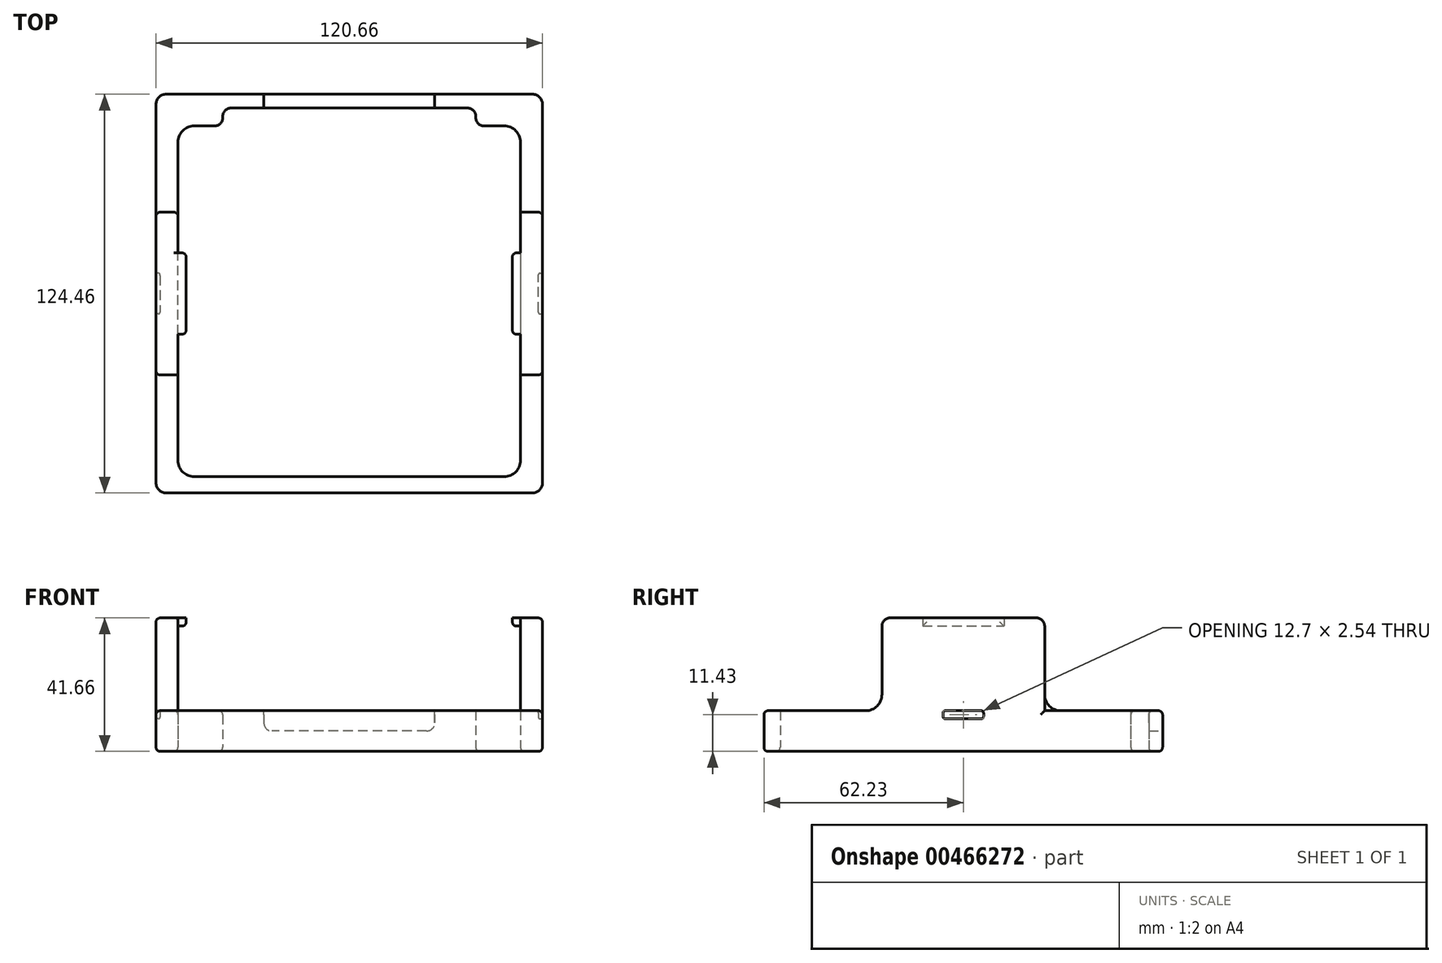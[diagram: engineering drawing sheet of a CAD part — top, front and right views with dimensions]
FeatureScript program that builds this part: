
annotation { "Feature Type Name" : "Feature", "Feature Type Description" : "" }
export const myFeature = defineFeature(function(context is Context, id is Id, definition is map)
    precondition{}
    {
        {
            var Q0;
            Q0=qCreatedBy(makeId("Top.planeOp"),FACE);
            var sketch = newSketch(context, id + "F0", { "sketchPlane" : qUnion([Q0])});
            skLineSegment(sketch, "E0.bottom", {"start": v(-57.15, -62.23) * mm, "end": v(57.15, -62.23) * mm});
            skLineSegment(sketch, "E0.top", {"start": v(-57.15, 62.23) * mm, "end": v(57.15, 62.23) * mm});
            skLineSegment(sketch, "E0.left", {"start": v(-60.32, -59.06) * mm, "end": v(-60.32, 59.06) * mm});
            skLineSegment(sketch, "E0.right", {"start": v(60.33, -59.06) * mm, "end": v(60.33, 59.06) * mm});
            skPoint(sketch, "E0.middle", {"position": v(0, 0) * mm});
            skPoint(sketch, "E1.visualSharp", {"position": v(55.25, 53.34) * mm});
            skPoint(sketch, "E2.visualSharp", {"position": v(60.33, 62.23) * mm});
            skArc(sketch, "E2.filletArc", {"start": v(60.33, 59.06) * mm, "mid": v(59.4, 61.3) * mm, "end": v(57.15, 62.23) * mm});
            skPoint(sketch, "E3.visualSharp", {"position": v(60.33, -62.23) * mm});
            skArc(sketch, "E3.filletArc", {"start": v(57.15, -62.23) * mm, "mid": v(59.4, -61.3) * mm, "end": v(60.33, -59.06) * mm});
            skPoint(sketch, "E4.visualSharp", {"position": v(-60.33, -62.23) * mm});
            skArc(sketch, "E4.filletArc", {"start": v(-60.33, -59.06) * mm, "mid": v(-59.4, -61.3) * mm, "end": v(-57.15, -62.23) * mm});
            skPoint(sketch, "E5.visualSharp", {"position": v(-60.32, 62.23) * mm});
            skArc(sketch, "E5.filletArc", {"start": v(-57.15, 62.23) * mm, "mid": v(-59.4, 61.3) * mm, "end": v(-60.32, 59.06) * mm});
            skLineSegment(sketch, "E6.bottom", {"start": v(48.39, 52.32) * mm, "end": v(39.5, 52.32) * mm});
            skLineSegment(sketch, "E6.top", {"start": v(48.39, -57.15) * mm, "end": v(-48.39, -57.15) * mm});
            skLineSegment(sketch, "E6.left", {"start": v(53.47, 47.24) * mm, "end": v(53.47, -52.07) * mm});
            skLineSegment(sketch, "E6.right", {"start": v(-53.47, 47.24) * mm, "end": v(-53.47, -52.07) * mm});
            skPoint(sketch, "E7.visualSharp", {"position": v(53.47, -57.15) * mm});
            skArc(sketch, "E7.filletArc", {"start": v(48.39, -57.15) * mm, "mid": v(51.98, -55.66) * mm, "end": v(53.47, -52.07) * mm});
            skPoint(sketch, "E8.visualSharp", {"position": v(-53.47, -57.15) * mm});
            skArc(sketch, "E8.filletArc", {"start": v(-53.47, -52.07) * mm, "mid": v(-51.98, -55.66) * mm, "end": v(-48.39, -57.15) * mm});
            skPoint(sketch, "E9.visualSharp", {"position": v(53.47, 52.32) * mm});
            skArc(sketch, "E9.filletArc", {"start": v(53.47, 47.24) * mm, "mid": v(51.98, 50.84) * mm, "end": v(48.39, 52.32) * mm});
            skPoint(sketch, "E10.visualSharp", {"position": v(-53.47, 52.32) * mm});
            skArc(sketch, "E10.filletArc", {"start": v(-48.39, 52.32) * mm, "mid": v(-51.98, 50.84) * mm, "end": v(-53.47, 47.24) * mm});
            skLineSegment(sketch, "E11.bottom", {"start": v(-39.5, 57.91) * mm, "end": v(39.5, 57.91) * mm});
            skLineSegment(sketch, "E11.left", {"start": v(-39.5, 57.91) * mm, "end": v(-39.5, 52.32) * mm});
            skLineSegment(sketch, "E11.right", {"start": v(39.5, 57.91) * mm, "end": v(39.5, 52.32) * mm});
            skLineSegment(sketch, "E12", {"start": v(0, 62.23) * mm, "end": v(0, 0) * mm, "construction": true});
            skPoint(sketch, "E12.endSnap0", {"position": v(0, 62.23) * mm});
            skPoint(sketch, "E13", {"position": v(0, 57.91) * mm});
            skLineSegment(sketch, "E14.trimOffspring", {"start": v(-39.5, 52.32) * mm, "end": v(-48.39, 52.32) * mm});
            skSolve(sketch);
        }
        {
            var Q0;
            Q0=makeQuery(id+"F0.imprint","IMPRINT",FACE,{"disambiguationData":[TD([[makeQuery(id+"F0.imprint","IMPRINT",EDGE,{"derivedFrom":sQuery(id+"F0.wireOp",EDGE,"E0.bottom")}),1.0]])]});
            extrude(context, id + "F1", {"entities" : qUnion([Q0]), "depth" : 12.7 * mm});
        }
        {
            var Q0;
            Q0=makeQuery(id+"F1.opExtrude","SWEPT_FACE",FACE,{"disambiguationData":[OSD([sQuery(id+"F0.wireOp",EDGE,"E0.top")])]});
            var sketch = newSketch(context, id + "F2", { "sketchPlane" : qUnion([Q0])});
            skPoint(sketch, "E15.firstSnap0", {"position": v(-57.15, 6.35) * mm});
            skLineSegment(sketch, "E15.bottom", {"start": v(-26.67, 6.35) * mm, "end": v(26.67, 6.35) * mm});
            skLineSegment(sketch, "E15.top", {"start": v(-26.67, 12.7) * mm, "end": v(26.67, 12.7) * mm});
            skLineSegment(sketch, "E15.left", {"start": v(-26.67, 12.7) * mm, "end": v(-26.67, 6.35) * mm});
            skLineSegment(sketch, "E15.right", {"start": v(26.67, 12.7) * mm, "end": v(26.67, 6.35) * mm});
            skPoint(sketch, "E16", {"position": v(0, 6.35) * mm});
            skLineSegment(sketch, "E17", {"start": v(0, 0) * mm, "end": v(0, 61.26) * mm, "construction": true});
            skPoint(sketch, "E17.endSnap0", {"position": v(0, 12.7) * mm});
            skSolve(sketch);
        }
        {
            var Q0;
            Q0 = qSketchRegion(id + "F2", true);
            var Q1;
            Q1=makeQuery(id+"F1.opExtrude","SWEPT_FACE",FACE,{"disambiguationData":[OSD([sQuery(id+"F0.wireOp",EDGE,"E11.bottom")])]});
            extrude(context, id + "F3", {"entities" : qUnion([Q0]), "operationType" : NewBodyOperationType.REMOVE, "endBound" : BoundingType.UP_TO_SURFACE, "oppositeDirection" : true, "endBoundEntityFace" : qUnion([Q1]), "depth" : 25.4 * mm});
        }
        {
            var Q0;
            Q0=makeQuery(id+"F1.opExtrude","CAP_FACE",FACE,{"disambiguationData":[OSD([sQuery(id+"F0.wireOp",EDGE,"E0.bottom"),sQuery(id+"F0.wireOp",EDGE,"E0.top"),sQuery(id+"F0.wireOp",EDGE,"E0.left"),sQuery(id+"F0.wireOp",EDGE,"E0.right"),sQuery(id+"F0.wireOp",EDGE,"E2.filletArc"),sQuery(id+"F0.wireOp",EDGE,"E3.filletArc"),sQuery(id+"F0.wireOp",EDGE,"E4.filletArc"),sQuery(id+"F0.wireOp",EDGE,"E5.filletArc"),sQuery(id+"F0.wireOp",EDGE,"E6.bottom"),sQuery(id+"F0.wireOp",EDGE,"E6.top"),sQuery(id+"F0.wireOp",EDGE,"E6.left"),sQuery(id+"F0.wireOp",EDGE,"E6.right"),sQuery(id+"F0.wireOp",EDGE,"E7.filletArc"),sQuery(id+"F0.wireOp",EDGE,"E8.filletArc"),sQuery(id+"F0.wireOp",EDGE,"E9.filletArc"),sQuery(id+"F0.wireOp",EDGE,"E10.filletArc"),sQuery(id+"F0.wireOp",EDGE,"E11.bottom"),sQuery(id+"F0.wireOp",EDGE,"E11.left"),sQuery(id+"F0.wireOp",EDGE,"E11.right"),sQuery(id+"F0.wireOp",EDGE,"E14.trimOffspring")])],"isStart":false});
            var sketch = newSketch(context, id + "F4", { "sketchPlane" : qUnion([Q0])});
            skLineSegment(sketch, "E18.bottom", {"start": v(60.33, -25.4) * mm, "end": v(53.47, -25.4) * mm});
            skLineSegment(sketch, "E18.top", {"start": v(60.33, 25.4) * mm, "end": v(53.47, 25.4) * mm});
            skLineSegment(sketch, "E18.left", {"start": v(60.33, -25.4) * mm, "end": v(60.33, 25.4) * mm});
            skLineSegment(sketch, "E18.right", {"start": v(53.47, -25.4) * mm, "end": v(53.47, 25.4) * mm});
            skLineSegment(sketch, "E19.bottom", {"start": v(-60.32, -25.4) * mm, "end": v(-53.47, -25.4) * mm});
            skLineSegment(sketch, "E19.top", {"start": v(-60.33, 25.4) * mm, "end": v(-53.47, 25.4) * mm});
            skLineSegment(sketch, "E19.left", {"start": v(-60.32, -25.4) * mm, "end": v(-60.32, 25.4) * mm});
            skLineSegment(sketch, "E19.right", {"start": v(-53.47, -25.4) * mm, "end": v(-53.47, 25.4) * mm});
            skSolve(sketch);
        }
        {
            var Q0;
            Q0 = qSketchRegion(id + "F4", true);
            extrude(context, id + "F5", {"entities" : qUnion([Q0]), "operationType" : NewBodyOperationType.ADD, "depth" : 28.96 * mm, "offsetDistance" : 25.4 * mm});
        }
        {
            var Q0;
            Q0=makeQuery(id+"F5.boolean.opBoolean","MERGE",FACE,{"derivedFrom":[makeQuery(id+"F1.opExtrude","SWEPT_FACE",FACE,{"disambiguationData":[OSD([sQuery(id+"F0.wireOp",EDGE,"E6.right")])]}),makeQuery(id+"F5.opExtrude","SWEPT_FACE",FACE,{"disambiguationData":[OSD([sQuery(id+"F4.wireOp",EDGE,"E19.right")])]})]});
            var sketch = newSketch(context, id + "F6", { "sketchPlane" : qUnion([Q0])});
            skLineSegment(sketch, "E20.bottom", {"start": v(-12.7, 41.66) * mm, "end": v(12.7, 41.66) * mm});
            skLineSegment(sketch, "E20.top", {"start": v(-12.7, 39.12) * mm, "end": v(12.7, 39.12) * mm});
            skLineSegment(sketch, "E20.left", {"start": v(-12.7, 41.66) * mm, "end": v(-12.7, 39.12) * mm});
            skLineSegment(sketch, "E20.right", {"start": v(12.7, 41.66) * mm, "end": v(12.7, 39.12) * mm});
            skSolve(sketch);
        }
        {
            var Q0;
            Q0=makeQuery(id+"F5.boolean.opBoolean","MERGE",FACE,{"derivedFrom":[makeQuery(id+"F1.opExtrude","SWEPT_FACE",FACE,{"disambiguationData":[OSD([sQuery(id+"F0.wireOp",EDGE,"E6.left")])]}),makeQuery(id+"F5.opExtrude","SWEPT_FACE",FACE,{"disambiguationData":[OSD([sQuery(id+"F4.wireOp",EDGE,"E18.right")])]})]});
            var sketch = newSketch(context, id + "F7", { "sketchPlane" : qUnion([Q0])});
            skLineSegment(sketch, "E21.bottom", {"start": v(-12.7, 41.66) * mm, "end": v(12.7, 41.66) * mm});
            skLineSegment(sketch, "E21.top", {"start": v(-12.7, 39.12) * mm, "end": v(12.7, 39.12) * mm});
            skLineSegment(sketch, "E21.left", {"start": v(-12.7, 41.66) * mm, "end": v(-12.7, 39.12) * mm});
            skLineSegment(sketch, "E21.right", {"start": v(12.7, 41.66) * mm, "end": v(12.7, 39.12) * mm});
            skSolve(sketch);
        }
        {
            var Q0;
            Q0=makeQuery(id+"F7.imprint","IMPRINT",FACE,{"disambiguationData":[TD([[makeQuery(id+"F7.imprint","IMPRINT",EDGE,{"derivedFrom":sQuery(id+"F7.wireOp",EDGE,"E21.bottom")}),-1.0]])]});
            extrude(context, id + "F8", {"entities" : qUnion([Q0]), "operationType" : NewBodyOperationType.ADD, "depth" : 2.54 * mm});
        }
        {
            var Q0;
            Q0=makeQuery(id+"F6.imprint","IMPRINT",FACE,{"disambiguationData":[TD([[makeQuery(id+"F6.imprint","IMPRINT",EDGE,{"derivedFrom":sQuery(id+"F6.wireOp",EDGE,"E20.bottom")}),1.0]])]});
            extrude(context, id + "F9", {"entities" : qUnion([Q0]), "operationType" : NewBodyOperationType.ADD, "depth" : 2.54 * mm});
        }
        {
            var Q0;
            Q0=makeQuery(id+"F5.opExtrude","CAP_EDGE",EDGE,{"disambiguationData":[OSD([sQuery(id+"F4.wireOp",EDGE,"E18.top")])],"isStart":true});
            var Q1;
            Q1=makeQuery(id+"F5.opExtrude","CAP_EDGE",EDGE,{"disambiguationData":[OSD([sQuery(id+"F4.wireOp",EDGE,"E19.top")])],"isStart":true});
            var Q2;
            Q2=makeQuery(id+"F5.opExtrude","CAP_EDGE",EDGE,{"disambiguationData":[OSD([sQuery(id+"F4.wireOp",EDGE,"E18.bottom")])],"isStart":true});
            var Q3;
            Q3=makeQuery(id+"F5.opExtrude","CAP_EDGE",EDGE,{"disambiguationData":[OSD([sQuery(id+"F4.wireOp",EDGE,"E19.bottom")])],"isStart":true});
            fillet(context, id + "F10", {"entities" : qUnion([Q0, Q1, Q2, Q3]), "radius" : 5.08 * mm, "tangentPropagation" : true, "allowEdgeOverflow" : false});
        }
        {
            var Q0;
            Q0=makeQuery(id+"F5.opExtrude","CAP_EDGE",EDGE,{"disambiguationData":[OSD([sQuery(id+"F4.wireOp",EDGE,"E19.bottom")])],"isStart":false});
            var Q1;
            Q1=makeQuery(id+"F5.opExtrude","CAP_EDGE",EDGE,{"disambiguationData":[OSD([sQuery(id+"F4.wireOp",EDGE,"E19.top")])],"isStart":false});
            var Q2;
            Q2=makeQuery(id+"F5.opExtrude","CAP_EDGE",EDGE,{"disambiguationData":[OSD([sQuery(id+"F4.wireOp",EDGE,"E18.bottom")])],"isStart":false});
            var Q3;
            Q3=makeQuery(id+"F5.opExtrude","CAP_EDGE",EDGE,{"disambiguationData":[OSD([sQuery(id+"F4.wireOp",EDGE,"E18.top")])],"isStart":false});
            fillet(context, id + "F11", {"entities" : qUnion([Q0, Q1, Q2, Q3]), "radius" : 2.54 * mm, "tangentPropagation" : true, "allowEdgeOverflow" : false});
        }
        {
            var Q0;
            Q0=makeQuery(id+"F9.opExtrude","CAP_EDGE",EDGE,{"disambiguationData":[OSD([sQuery(id+"F6.wireOp",EDGE,"E20.left")])],"isStart":false});
            var Q1;
            Q1=makeQuery(id+"F9.opExtrude","CAP_EDGE",EDGE,{"disambiguationData":[OSD([sQuery(id+"F6.wireOp",EDGE,"E20.right")])],"isStart":false});
            var Q2;
            Q2=makeQuery(id+"F8.opExtrude","CAP_EDGE",EDGE,{"disambiguationData":[OSD([sQuery(id+"F7.wireOp",EDGE,"E21.left")])],"isStart":false});
            var Q3;
            Q3=makeQuery(id+"F8.opExtrude","CAP_EDGE",EDGE,{"disambiguationData":[OSD([sQuery(id+"F7.wireOp",EDGE,"E21.right")])],"isStart":false});
            var Q4;
            Q4=makeQuery(id+"F8.opExtrude","CAP_EDGE",EDGE,{"disambiguationData":[OSD([sQuery(id+"F7.wireOp",EDGE,"E21.top")])],"isStart":true});
            var Q5;
            Q5=makeQuery(id+"F9.opExtrude","CAP_EDGE",EDGE,{"disambiguationData":[OSD([sQuery(id+"F6.wireOp",EDGE,"E20.top")])],"isStart":true});
            var Q6;
            Q6=makeQuery(id+"F9.opExtrude","CAP_EDGE",EDGE,{"disambiguationData":[OSD([sQuery(id+"F6.wireOp",EDGE,"E20.right")])],"isStart":true});
            var Q7;
            Q7=makeQuery(id+"F8.opExtrude","CAP_EDGE",EDGE,{"disambiguationData":[OSD([sQuery(id+"F7.wireOp",EDGE,"E21.left")])],"isStart":true});
            var Q8;
            Q8=makeQuery(id+"F8.opExtrude","CAP_EDGE",EDGE,{"disambiguationData":[OSD([sQuery(id+"F7.wireOp",EDGE,"E21.right")])],"isStart":true});
            var Q9;
            Q9=makeQuery(id+"F9.opExtrude","CAP_EDGE",EDGE,{"disambiguationData":[OSD([sQuery(id+"F6.wireOp",EDGE,"E20.left")])],"isStart":true});
            var Q10;
            Q10=makeQuery(id+"F8.opExtrude","CAP_EDGE",EDGE,{"disambiguationData":[OSD([sQuery(id+"F7.wireOp",EDGE,"E21.top")])],"isStart":false});
            var Q11;
            Q11=makeQuery(id+"F9.opExtrude","CAP_EDGE",EDGE,{"disambiguationData":[OSD([sQuery(id+"F6.wireOp",EDGE,"E20.top")])],"isStart":false});
            fillet(context, id + "F12", {"entities" : qUnion([Q0, Q1, Q2, Q3, Q4, Q5, Q6, Q7, Q8, Q9, Q10, Q11]), "radius" : 1.27 * mm, "tangentPropagation" : true, "allowEdgeOverflow" : false});
        }
        {
            var Q0;
            Q0=makeQuery(id+"F1.opExtrude","SWEPT_EDGE",EDGE,{"disambiguationData":[OSD([sQuery(id+"F0.wireOp",EDGE,"E11.left"),sQuery(id+"F0.wireOp",EDGE,"E14.trimOffspring")])]});
            var Q1;
            Q1=makeQuery(id+"F3.boolean.opBoolean","COPY",EDGE,{"derivedFrom":makeQuery(id+"F3.opExtrude","SWEPT_EDGE",EDGE,{"disambiguationData":[OSD([sQuery(id+"F0.wireOp",EDGE,"E0.top"),sQuery(id+"F2.wireOp",EDGE,"E15.top"),sQuery(id+"F2.wireOp",EDGE,"E15.right")])]})});
            var Q2;
            Q2=makeQuery(id+"F3.boolean.opBoolean","COPY",EDGE,{"derivedFrom":makeQuery(id+"F3.opExtrude","SWEPT_EDGE",EDGE,{"disambiguationData":[OSD([sQuery(id+"F0.wireOp",EDGE,"E0.top"),sQuery(id+"F2.wireOp",EDGE,"E15.top"),sQuery(id+"F2.wireOp",EDGE,"E15.left")])]})});
            var Q3;
            Q3=makeQuery(id+"F1.opExtrude","SWEPT_EDGE",EDGE,{"disambiguationData":[OSD([sQuery(id+"F0.wireOp",EDGE,"E6.bottom"),sQuery(id+"F0.wireOp",EDGE,"E11.right")])]});
            var Q4;
            Q4=makeQuery(id+"F1.opExtrude","SWEPT_EDGE",EDGE,{"disambiguationData":[OSD([sQuery(id+"F0.wireOp",EDGE,"E11.bottom"),sQuery(id+"F0.wireOp",EDGE,"E11.left")])]});
            var Q5;
            Q5=makeQuery(id+"F1.opExtrude","SWEPT_EDGE",EDGE,{"disambiguationData":[OSD([sQuery(id+"F0.wireOp",EDGE,"E11.bottom"),sQuery(id+"F0.wireOp",EDGE,"E11.right")])]});
            var Q6;
            Q6=makeQuery(id+"F3.boolean.opBoolean","COPY",EDGE,{"derivedFrom":makeQuery(id+"F3.opExtrude","SWEPT_EDGE",EDGE,{"disambiguationData":[OSD([sQuery(id+"F2.wireOp",EDGE,"E15.bottom"),sQuery(id+"F2.wireOp",EDGE,"E15.left")])]})});
            var Q7;
            Q7=makeQuery(id+"F3.boolean.opBoolean","COPY",EDGE,{"derivedFrom":makeQuery(id+"F3.opExtrude","SWEPT_EDGE",EDGE,{"disambiguationData":[OSD([sQuery(id+"F2.wireOp",EDGE,"E15.bottom"),sQuery(id+"F2.wireOp",EDGE,"E15.right")])]})});
            fillet(context, id + "F13", {"entities" : qUnion([Q0, Q1, Q2, Q3, Q4, Q5, Q6, Q7]), "radius" : 2.54 * mm, "tangentPropagation" : true, "allowEdgeOverflow" : false});
        }
        {
            var Q0;
            {var subQ0=sQuery(id+"F0.wireOp",EDGE,"E6.right");var subQ1=sQuery(id+"F0.wireOp",EDGE,"E10.filletArc");Q0=makeQuery(id+"F5.boolean.opBoolean","SPLIT",EDGE,{"disambiguationData":[TD([makeQuery(id+"F1.opExtrude","SWEPT_FACE",FACE,{"disambiguationData":[OSD([subQ1])]})])],"derivedFrom":makeQuery(id+"F1.opExtrude","CAP_EDGE",EDGE,{"disambiguationData":[OSD([subQ0])],"isStart":false})});}
            var Q1;
            Q1=makeQuery(id+"F1.opExtrude","CAP_EDGE",EDGE,{"disambiguationData":[OSD([sQuery(id+"F0.wireOp",EDGE,"E10.filletArc")])],"isStart":false});
            var Q2;
            {var subQ0=sQuery(id+"F0.wireOp",EDGE,"E2.filletArc");var subQ1=sQuery(id+"F0.wireOp",EDGE,"E0.right");Q2=makeQuery(id+"F5.boolean.opBoolean","SPLIT",EDGE,{"disambiguationData":[TD([makeQuery(id+"F1.opExtrude","SWEPT_FACE",FACE,{"disambiguationData":[OSD([subQ0])]})])],"derivedFrom":makeQuery(id+"F1.opExtrude","CAP_EDGE",EDGE,{"disambiguationData":[OSD([subQ1])],"isStart":false})});}
            var Q3;
            Q3=makeQuery(id+"F1.opExtrude","CAP_EDGE",EDGE,{"disambiguationData":[OSD([sQuery(id+"F0.wireOp",EDGE,"E0.top")])],"isStart":false});
            var Q4;
            Q4=makeQuery(id+"F1.opExtrude","CAP_EDGE",EDGE,{"disambiguationData":[OSD([sQuery(id+"F0.wireOp",EDGE,"E2.filletArc")])],"isStart":false});
            var Q5;
            Q5=makeQuery(id+"F1.opExtrude","CAP_EDGE",EDGE,{"disambiguationData":[OSD([sQuery(id+"F0.wireOp",EDGE,"E5.filletArc")])],"isStart":false});
            var Q6;
            {var subQ0=sQuery(id+"F0.wireOp",EDGE,"E0.left");var subQ1=sQuery(id+"F0.wireOp",EDGE,"E5.filletArc");Q6=makeQuery(id+"F5.boolean.opBoolean","SPLIT",EDGE,{"disambiguationData":[TD([makeQuery(id+"F1.opExtrude","SWEPT_FACE",FACE,{"disambiguationData":[OSD([subQ1])]})])],"derivedFrom":makeQuery(id+"F1.opExtrude","CAP_EDGE",EDGE,{"disambiguationData":[OSD([subQ0])],"isStart":false})});}
            var Q7;
            Q7=makeQuery(id+"F1.opExtrude","CAP_EDGE",EDGE,{"disambiguationData":[OSD([sQuery(id+"F0.wireOp",EDGE,"E0.right")])],"isStart":true});
            var Q8;
            Q8=makeQuery(id+"F1.opExtrude","CAP_EDGE",EDGE,{"disambiguationData":[OSD([sQuery(id+"F0.wireOp",EDGE,"E2.filletArc")])],"isStart":true});
            fillet(context, id + "F14", {"entities" : qUnion([Q0, Q1, Q2, Q3, Q4, Q5, Q6, Q7, Q8]), "radius" : 1.27 * mm, "tangentPropagation" : true, "allowEdgeOverflow" : false});
        }
        {
            var Q0;
            Q0=makeQuery(id+"F1.opExtrude","CAP_EDGE",EDGE,{"disambiguationData":[OSD([sQuery(id+"F0.wireOp",EDGE,"E14.trimOffspring")])],"isStart":true});
            var Q1;
            {var subQ0=sQuery(id+"F0.wireOp",EDGE,"E14.trimOffspring");var subQ1=sQuery(id+"F0.wireOp",EDGE,"E11.left");Q1=makeQuery(id+"F13.opFillet","BLEND_EDGE",EDGE,{"blendedFrom":[makeQuery(id+"F1.opExtrude","SWEPT_EDGE",EDGE,{"disambiguationData":[OSD([subQ1,subQ0])]}),makeQuery(id+"F1.opExtrude","CAP_FACE",FACE,{"disambiguationData":[OSD([sQuery(id+"F0.wireOp",EDGE,"E0.bottom"),sQuery(id+"F0.wireOp",EDGE,"E0.top"),sQuery(id+"F0.wireOp",EDGE,"E0.left"),sQuery(id+"F0.wireOp",EDGE,"E0.right"),sQuery(id+"F0.wireOp",EDGE,"E2.filletArc"),sQuery(id+"F0.wireOp",EDGE,"E3.filletArc"),sQuery(id+"F0.wireOp",EDGE,"E4.filletArc"),sQuery(id+"F0.wireOp",EDGE,"E5.filletArc"),sQuery(id+"F0.wireOp",EDGE,"E6.bottom"),sQuery(id+"F0.wireOp",EDGE,"E6.top"),sQuery(id+"F0.wireOp",EDGE,"E6.left"),sQuery(id+"F0.wireOp",EDGE,"E6.right"),sQuery(id+"F0.wireOp",EDGE,"E7.filletArc"),sQuery(id+"F0.wireOp",EDGE,"E8.filletArc"),sQuery(id+"F0.wireOp",EDGE,"E9.filletArc"),sQuery(id+"F0.wireOp",EDGE,"E10.filletArc"),sQuery(id+"F0.wireOp",EDGE,"E11.bottom"),subQ1,sQuery(id+"F0.wireOp",EDGE,"E11.right"),subQ0])],"isStart":true})],"blendedInto":[makeQuery(id+"F1.opExtrude","CAP_FACE",FACE,{"disambiguationData":[OSD([sQuery(id+"F0.wireOp",EDGE,"E0.bottom"),sQuery(id+"F0.wireOp",EDGE,"E0.top"),sQuery(id+"F0.wireOp",EDGE,"E0.left"),sQuery(id+"F0.wireOp",EDGE,"E0.right"),sQuery(id+"F0.wireOp",EDGE,"E2.filletArc"),sQuery(id+"F0.wireOp",EDGE,"E3.filletArc"),sQuery(id+"F0.wireOp",EDGE,"E4.filletArc"),sQuery(id+"F0.wireOp",EDGE,"E5.filletArc"),sQuery(id+"F0.wireOp",EDGE,"E6.bottom"),sQuery(id+"F0.wireOp",EDGE,"E6.top"),sQuery(id+"F0.wireOp",EDGE,"E6.left"),sQuery(id+"F0.wireOp",EDGE,"E6.right"),sQuery(id+"F0.wireOp",EDGE,"E7.filletArc"),sQuery(id+"F0.wireOp",EDGE,"E8.filletArc"),sQuery(id+"F0.wireOp",EDGE,"E9.filletArc"),sQuery(id+"F0.wireOp",EDGE,"E10.filletArc"),sQuery(id+"F0.wireOp",EDGE,"E11.bottom"),subQ1,sQuery(id+"F0.wireOp",EDGE,"E11.right"),subQ0])],"isStart":true})]});}
            fillet(context, id + "F15", {"entities" : qUnion([Q0, Q1]), "radius" : 1.27 * mm, "tangentPropagation" : true, "allowEdgeOverflow" : false});
        }
        {
            var Q0;
            Q0=makeQuery(id+"F5.boolean.opBoolean","MERGE",FACE,{"derivedFrom":[makeQuery(id+"F1.opExtrude","SWEPT_FACE",FACE,{"disambiguationData":[OSD([sQuery(id+"F0.wireOp",EDGE,"E0.left")])]}),makeQuery(id+"F5.opExtrude","SWEPT_FACE",FACE,{"disambiguationData":[OSD([sQuery(id+"F4.wireOp",EDGE,"E19.left")])]})]});
            var sketch = newSketch(context, id + "F16", { "sketchPlane" : qUnion([Q0])});
            skLineSegment(sketch, "E22.bottom", {"start": v(-6.35, 12.7) * mm, "end": v(6.35, 12.7) * mm});
            skLineSegment(sketch, "E22.top", {"start": v(-6.35, 10.16) * mm, "end": v(6.35, 10.16) * mm});
            skLineSegment(sketch, "E22.left", {"start": v(-6.35, 12.7) * mm, "end": v(-6.35, 10.16) * mm});
            skLineSegment(sketch, "E22.right", {"start": v(6.35, 12.7) * mm, "end": v(6.35, 10.16) * mm});
            skSolve(sketch);
        }
        {
            var Q0;
            Q0=makeQuery(id+"F5.boolean.opBoolean","MERGE",FACE,{"derivedFrom":[makeQuery(id+"F1.opExtrude","SWEPT_FACE",FACE,{"disambiguationData":[OSD([sQuery(id+"F0.wireOp",EDGE,"E0.right")])]}),makeQuery(id+"F5.opExtrude","SWEPT_FACE",FACE,{"disambiguationData":[OSD([sQuery(id+"F4.wireOp",EDGE,"E18.left")])]})]});
            var sketch = newSketch(context, id + "F17", { "sketchPlane" : qUnion([Q0])});
            skPoint(sketch, "E23.firstSnap0", {"position": v(-25.99, 12.7) * mm});
            skLineSegment(sketch, "E23.bottom", {"start": v(-6.35, 12.7) * mm, "end": v(6.35, 12.7) * mm});
            skLineSegment(sketch, "E23.top", {"start": v(-6.35, 10.16) * mm, "end": v(6.35, 10.16) * mm});
            skLineSegment(sketch, "E23.left", {"start": v(-6.35, 12.7) * mm, "end": v(-6.35, 10.16) * mm});
            skLineSegment(sketch, "E23.right", {"start": v(6.35, 12.7) * mm, "end": v(6.35, 10.16) * mm});
            skSolve(sketch);
        }
        {
            var Q0;
            Q0=makeQuery(id+"F16.imprint","IMPRINT",FACE,{"disambiguationData":[TD([[makeQuery(id+"F16.imprint","IMPRINT",EDGE,{"derivedFrom":sQuery(id+"F16.wireOp",EDGE,"E22.bottom")}),-1.0]])]});
            extrude(context, id + "F18", {"entities" : qUnion([Q0]), "operationType" : NewBodyOperationType.REMOVE, "oppositeDirection" : true, "depth" : 1.27 * mm});
        }
        {
            var Q0;
            Q0=makeQuery(id+"F17.imprint","IMPRINT",FACE,{"disambiguationData":[TD([[makeQuery(id+"F17.imprint","IMPRINT",EDGE,{"derivedFrom":sQuery(id+"F17.wireOp",EDGE,"E23.bottom")}),-1.0]])]});
            extrude(context, id + "F19", {"entities" : qUnion([Q0]), "operationType" : NewBodyOperationType.REMOVE, "oppositeDirection" : true, "depth" : 1.27 * mm});
        }
        {
            var Q0;
            Q0=makeQuery(id+"F18.boolean.opBoolean","COPY",EDGE,{"derivedFrom":makeQuery(id+"F18.opExtrude","CAP_EDGE",EDGE,{"disambiguationData":[OSD([sQuery(id+"F16.wireOp",EDGE,"E22.top")])],"isStart":false})});
            var Q1;
            Q1=makeQuery(id+"F18.boolean.opBoolean","COPY",EDGE,{"derivedFrom":makeQuery(id+"F18.opExtrude","CAP_EDGE",EDGE,{"disambiguationData":[OSD([sQuery(id+"F16.wireOp",EDGE,"E22.left")])],"isStart":false})});
            var Q2;
            Q2=makeQuery(id+"F18.boolean.opBoolean","COPY",EDGE,{"derivedFrom":makeQuery(id+"F18.opExtrude","CAP_EDGE",EDGE,{"disambiguationData":[OSD([sQuery(id+"F16.wireOp",EDGE,"E22.bottom")])],"isStart":false})});
            var Q3;
            Q3=makeQuery(id+"F18.boolean.opBoolean","COPY",EDGE,{"derivedFrom":makeQuery(id+"F18.opExtrude","CAP_EDGE",EDGE,{"disambiguationData":[OSD([sQuery(id+"F16.wireOp",EDGE,"E22.right")])],"isStart":false})});
            var Q4;
            Q4=makeQuery(id+"F19.boolean.opBoolean","COPY",FACE,{"derivedFrom":makeQuery(id+"F19.opExtrude","CAP_FACE",FACE,{"disambiguationData":[OSD([sQuery(id+"F17.wireOp",EDGE,"E23.bottom"),sQuery(id+"F17.wireOp",EDGE,"E23.top"),sQuery(id+"F17.wireOp",EDGE,"E23.left"),sQuery(id+"F17.wireOp",EDGE,"E23.right")])],"isStart":false})});
            fillet(context, id + "F20", {"entities" : qUnion([Q0, Q1, Q2, Q3, Q4]), "radius" : 0.5 * mm, "tangentPropagation" : true, "allowEdgeOverflow" : false});
        }
        {
            var Q0;
            Q0=makeQuery(id+"F19.boolean.opBoolean","COPY",EDGE,{"derivedFrom":makeQuery(id+"F19.opExtrude","SWEPT_EDGE",EDGE,{"disambiguationData":[OSD([sQuery(id+"F17.wireOp",EDGE,"E23.top"),sQuery(id+"F17.wireOp",EDGE,"E23.left")])]})});
            var Q1;
            Q1=makeQuery(id+"F19.boolean.opBoolean","COPY",EDGE,{"derivedFrom":makeQuery(id+"F19.opExtrude","SWEPT_EDGE",EDGE,{"disambiguationData":[OSD([sQuery(id+"F17.wireOp",EDGE,"E23.bottom"),sQuery(id+"F17.wireOp",EDGE,"E23.left")])]})});
            var Q2;
            Q2=makeQuery(id+"F19.boolean.opBoolean","COPY",EDGE,{"derivedFrom":makeQuery(id+"F19.opExtrude","SWEPT_EDGE",EDGE,{"disambiguationData":[OSD([sQuery(id+"F17.wireOp",EDGE,"E23.bottom"),sQuery(id+"F17.wireOp",EDGE,"E23.right")])]})});
            var Q3;
            Q3=makeQuery(id+"F19.boolean.opBoolean","COPY",EDGE,{"derivedFrom":makeQuery(id+"F19.opExtrude","SWEPT_EDGE",EDGE,{"disambiguationData":[OSD([sQuery(id+"F17.wireOp",EDGE,"E23.top"),sQuery(id+"F17.wireOp",EDGE,"E23.right")])]})});
            var Q4;
            Q4=makeQuery(id+"F20.opFillet","BLEND_EDGE",EDGE,{"blendedFrom":[makeQuery(id+"F18.boolean.opBoolean","COPY",EDGE,{"derivedFrom":makeQuery(id+"F18.opExtrude","CAP_EDGE",EDGE,{"disambiguationData":[OSD([sQuery(id+"F16.wireOp",EDGE,"E22.bottom")])],"isStart":false})}),makeQuery(id+"F18.boolean.opBoolean","COPY",EDGE,{"derivedFrom":makeQuery(id+"F18.opExtrude","CAP_EDGE",EDGE,{"disambiguationData":[OSD([sQuery(id+"F16.wireOp",EDGE,"E22.left")])],"isStart":false})})],"blendedInto":[]});
            var Q5;
            Q5=makeQuery(id+"F20.opFillet","BLEND_EDGE",EDGE,{"blendedFrom":[makeQuery(id+"F18.boolean.opBoolean","COPY",EDGE,{"derivedFrom":makeQuery(id+"F18.opExtrude","CAP_EDGE",EDGE,{"disambiguationData":[OSD([sQuery(id+"F16.wireOp",EDGE,"E22.top")])],"isStart":false})}),makeQuery(id+"F18.boolean.opBoolean","COPY",EDGE,{"derivedFrom":makeQuery(id+"F18.opExtrude","CAP_EDGE",EDGE,{"disambiguationData":[OSD([sQuery(id+"F16.wireOp",EDGE,"E22.left")])],"isStart":false})})],"blendedInto":[]});
            var Q6;
            Q6=makeQuery(id+"F20.opFillet","BLEND_EDGE",EDGE,{"blendedFrom":[makeQuery(id+"F18.boolean.opBoolean","COPY",EDGE,{"derivedFrom":makeQuery(id+"F18.opExtrude","CAP_EDGE",EDGE,{"disambiguationData":[OSD([sQuery(id+"F16.wireOp",EDGE,"E22.bottom")])],"isStart":false})}),makeQuery(id+"F18.boolean.opBoolean","COPY",EDGE,{"derivedFrom":makeQuery(id+"F18.opExtrude","CAP_EDGE",EDGE,{"disambiguationData":[OSD([sQuery(id+"F16.wireOp",EDGE,"E22.right")])],"isStart":false})})],"blendedInto":[]});
            var Q7;
            Q7=makeQuery(id+"F20.opFillet","BLEND_EDGE",EDGE,{"blendedFrom":[makeQuery(id+"F18.boolean.opBoolean","COPY",EDGE,{"derivedFrom":makeQuery(id+"F18.opExtrude","CAP_EDGE",EDGE,{"disambiguationData":[OSD([sQuery(id+"F16.wireOp",EDGE,"E22.top")])],"isStart":false})}),makeQuery(id+"F18.boolean.opBoolean","COPY",EDGE,{"derivedFrom":makeQuery(id+"F18.opExtrude","CAP_EDGE",EDGE,{"disambiguationData":[OSD([sQuery(id+"F16.wireOp",EDGE,"E22.right")])],"isStart":false})})],"blendedInto":[]});
            fillet(context, id + "F21", {"entities" : qUnion([Q0, Q1, Q2, Q3, Q4, Q5, Q6, Q7]), "radius" : 0.76 * mm, "tangentPropagation" : true, "allowEdgeOverflow" : false});
        }
    });
